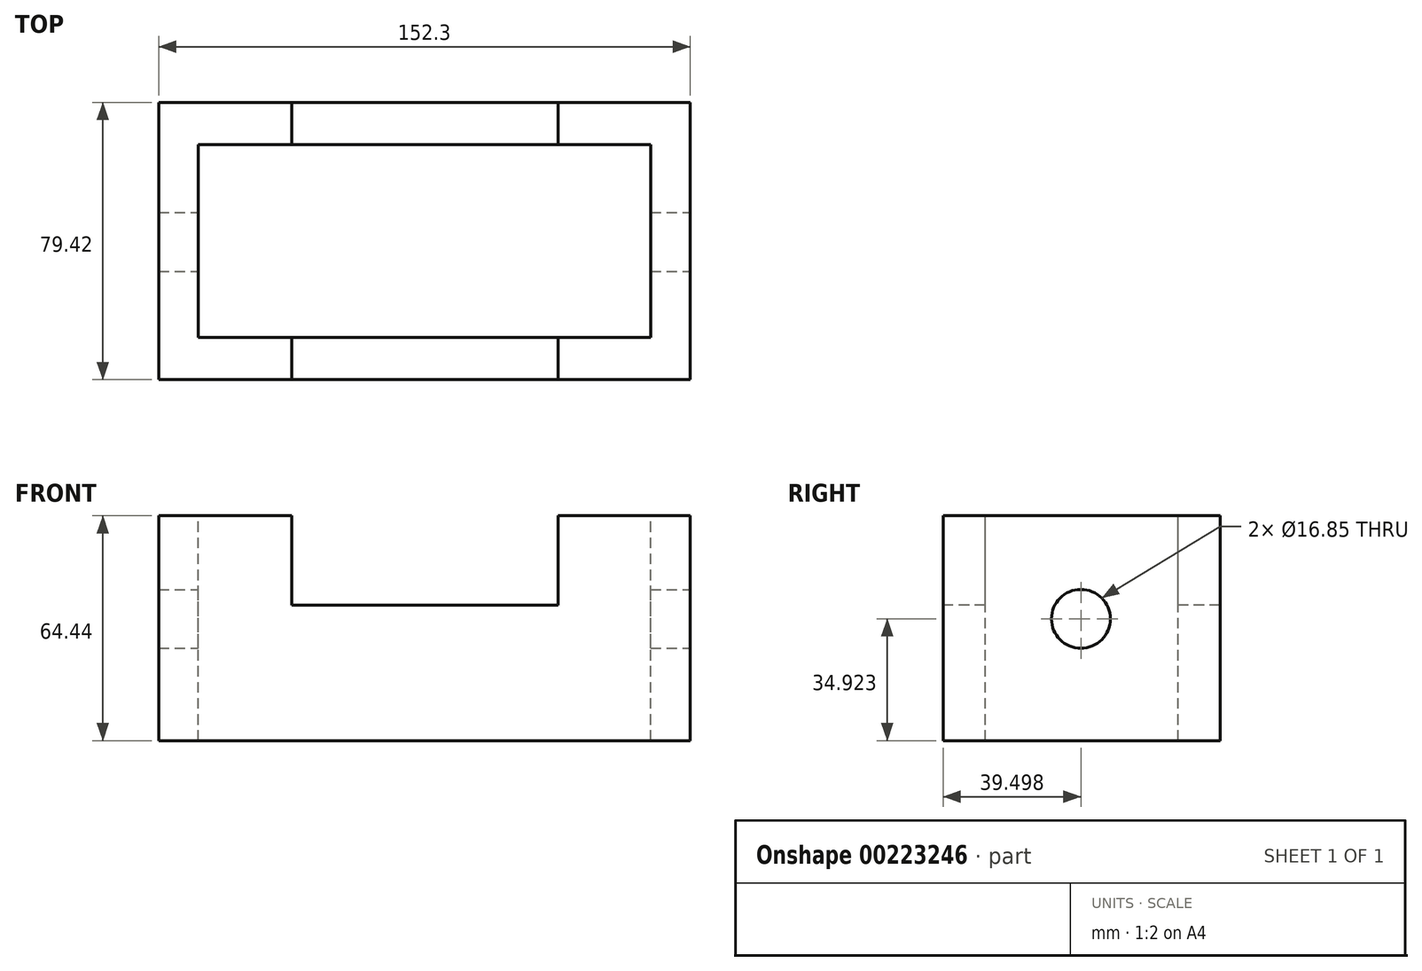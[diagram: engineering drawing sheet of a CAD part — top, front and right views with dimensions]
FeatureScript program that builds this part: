
annotation { "Feature Type Name" : "Feature", "Feature Type Description" : "" }
export const myFeature = defineFeature(function(context is Context, id is Id, definition is map)
    precondition{}
    {
        {
            var Q0;
            Q0=qCreatedBy(makeId("Top.planeOp"),FACE);
            var sketch = newSketch(context, id + "F0", { "sketchPlane" : qUnion([Q0])});
            skLineSegment(sketch, "E0.bottom", {"start": v(76.15, -39.7) * mm, "end": v(-76.15, -39.7) * mm});
            skLineSegment(sketch, "E0.top", {"start": v(76.15, 39.7) * mm, "end": v(-76.15, 39.7) * mm});
            skLineSegment(sketch, "E0.left", {"start": v(76.15, -39.7) * mm, "end": v(76.15, 39.7) * mm});
            skLineSegment(sketch, "E0.right", {"start": v(-76.15, -39.7) * mm, "end": v(-76.15, 39.7) * mm});
            skPoint(sketch, "E0.middle", {"position": v(0, 0) * mm});
            skSolve(sketch);
        }
        {
            var Q0;
            Q0=makeQuery(id+"F0.imprint","IMPRINT",FACE,{"disambiguationData":[TD([[makeQuery(id+"F0.imprint","IMPRINT",EDGE,{"derivedFrom":sQuery(id+"F0.wireOp",EDGE,"E0.bottom")}),-1.0]])]});
            extrude(context, id + "F1", {"entities" : qUnion([Q0]), "depth" : 64.44 * mm});
        }
        {
            var Q0;
            Q0=makeQuery(id+"F1.opExtrude","CAP_FACE",FACE,{"disambiguationData":[OSD([sQuery(id+"F0.wireOp",EDGE,"E0.bottom"),sQuery(id+"F0.wireOp",EDGE,"E0.top"),sQuery(id+"F0.wireOp",EDGE,"E0.left"),sQuery(id+"F0.wireOp",EDGE,"E0.right")])],"isStart":false});
            var sketch = newSketch(context, id + "F2", { "sketchPlane" : qUnion([Q0])});
            skLineSegment(sketch, "E1.bottom", {"start": v(64.8, -27.62) * mm, "end": v(-64.8, -27.62) * mm});
            skLineSegment(sketch, "E1.top", {"start": v(64.8, 27.62) * mm, "end": v(-64.8, 27.62) * mm});
            skLineSegment(sketch, "E1.left", {"start": v(64.8, -27.62) * mm, "end": v(64.8, 27.62) * mm});
            skLineSegment(sketch, "E1.right", {"start": v(-64.8, -27.62) * mm, "end": v(-64.8, 27.62) * mm});
            skPoint(sketch, "E1.middle", {"position": v(0, 0) * mm});
            skSolve(sketch);
        }
        {
            var Q0;
            Q0=makeQuery(id+"F2.imprint","IMPRINT",FACE,{"disambiguationData":[TD([[makeQuery(id+"F2.imprint","IMPRINT",EDGE,{"derivedFrom":sQuery(id+"F2.wireOp",EDGE,"E1.bottom")}),-1.0]])]});
            extrude(context, id + "F3", {"entities" : qUnion([Q0]), "operationType" : NewBodyOperationType.REMOVE, "endBound" : BoundingType.THROUGH_ALL, "oppositeDirection" : true, "depth" : 25.4 * mm});
        }
        {
            var Q0;
            Q0=makeQuery(id+"F1.opExtrude","SWEPT_FACE",FACE,{"disambiguationData":[OSD([sQuery(id+"F0.wireOp",EDGE,"E0.bottom")])]});
            var sketch = newSketch(context, id + "F7", { "sketchPlane" : qUnion([Q0])});
            skLineSegment(sketch, "E2.bottom", {"start": v(-38, 64.44) * mm, "end": v(38.33, 64.44) * mm});
            skLineSegment(sketch, "E2.top", {"start": v(-38, 38.89) * mm, "end": v(38.33, 38.89) * mm});
            skLineSegment(sketch, "E2.left", {"start": v(-38, 64.44) * mm, "end": v(-38, 38.89) * mm});
            skLineSegment(sketch, "E2.right", {"start": v(38.33, 64.44) * mm, "end": v(38.33, 38.89) * mm});
            skSolve(sketch);
        }
        {
            var Q0;
            Q0=makeQuery(id+"F7.imprint","IMPRINT",FACE,{"disambiguationData":[TD([[makeQuery(id+"F7.imprint","IMPRINT",EDGE,{"derivedFrom":sQuery(id+"F7.wireOp",EDGE,"E2.bottom")}),1.0]])]});
            extrude(context, id + "F4", {"entities" : qUnion([Q0]), "operationType" : NewBodyOperationType.REMOVE, "endBound" : BoundingType.THROUGH_ALL, "oppositeDirection" : true, "depth" : 25.4 * mm});
        }
        {
            var Q0;
            Q0=makeQuery(id+"F1.opExtrude","SWEPT_FACE",FACE,{"disambiguationData":[OSD([sQuery(id+"F0.wireOp",EDGE,"E0.left")])]});
            var sketch = newSketch(context, id + "F5", { "sketchPlane" : qUnion([Q0])});
            skCircle(sketch, "E3", {"center": v(-0.21, 34.92) * mm, "radius": 8.43 * mm});
            skSolve(sketch);
        }
        {
            var Q0;
            Q0=makeQuery(id+"F5.imprint","IMPRINT",FACE,{"disambiguationData":[TD([[makeQuery(id+"F5.imprint","IMPRINT",EDGE,{"derivedFrom":sQuery(id+"F5.wireOp",EDGE,"E3")}),1.0]])]});
            extrude(context, id + "F6", {"entities" : qUnion([Q0]), "operationType" : NewBodyOperationType.REMOVE, "endBound" : BoundingType.THROUGH_ALL, "oppositeDirection" : true, "depth" : 25.4 * mm});
        }
    });
